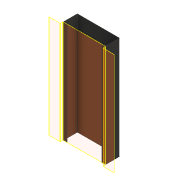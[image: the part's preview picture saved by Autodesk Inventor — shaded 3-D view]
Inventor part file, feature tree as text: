
AUTODESK INVENTOR PART (.ipt)
format: ipt  version: 2018 (Build 220112000, 112)  size: 155,136 bytes
history: native  units: mm
features: other x5, sheet_metal_op x3, sketch x1
ambient origin geometry x8: Origin, YZ Plane, XZ Plane, XY Plane, X Axis, Y Axis, Z Axis, Center Point
bodies: Solid1 (feature_tree)
feature tree (9):
  other  "20-001-CASE.ipt"
  sheet_metal_op  "Contour Flange1"
  other  "TaggingFeature1"
  sketch  "Sketch1"  dims[d0=10.0mm d1=226.0mm d2=20.0mm d3=75.0mm d4=1.0mm d5=1.0mm d6=0.5mm d7=2.0mm d8=1.0mm d9=550.0mm d10=1.0mm d11=1.0mm d12=4.0mm d13=1.0mm d14=1.0mm]
  other  "Plate1"
  sheet_metal_op  "Bend1"
  sheet_metal_op  "Corner1"
  other  "Solid1::20-001-CASE.ipt"
  other  "Srf1"
